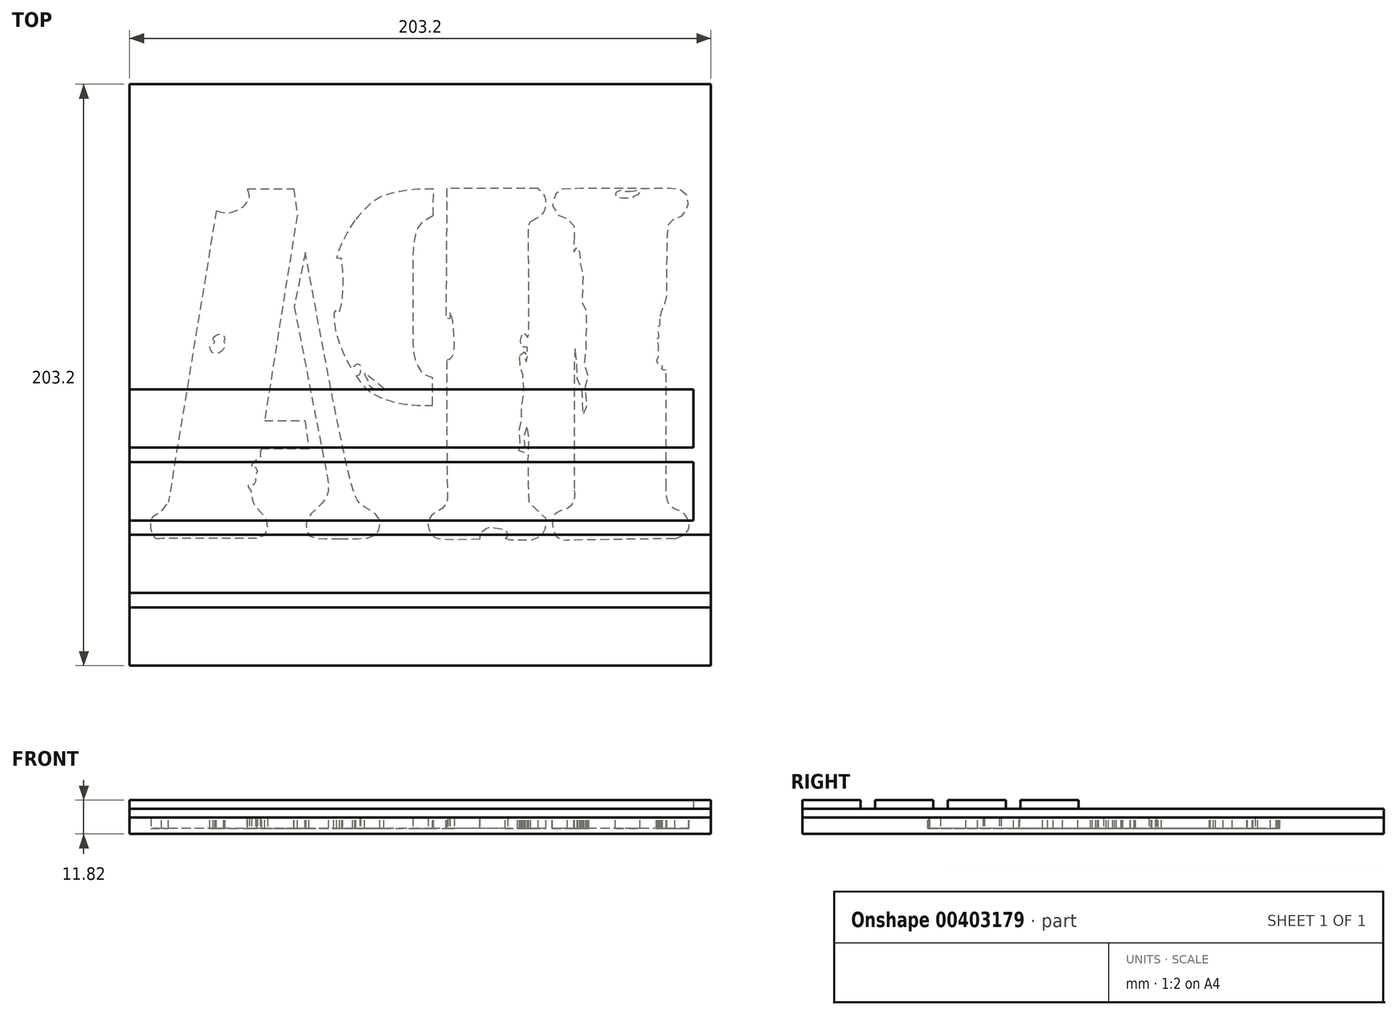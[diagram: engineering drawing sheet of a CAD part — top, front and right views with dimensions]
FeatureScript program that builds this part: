
annotation { "Feature Type Name" : "Feature", "Feature Type Description" : "" }
export const myFeature = defineFeature(function(context is Context, id is Id, definition is map)
    precondition{}
    {
        {
            var Q0;
            Q0=qCreatedBy(makeId("Top.planeOp"),FACE);
            var sketch = newSketch(context, id + "F0", { "sketchPlane" : qUnion([Q0])});
            skFitSpline(sketch, "E0", {"points": [v(8.63, 10.99) * mm, v(3.16, 11.1) * mm, v(2.03, 11.78) * mm, v(1.93, 12.44) * mm, v(2.34, 13.27) * mm, v(3.2, 13.72) * mm, v(3.76, 14.27) * mm, v(3.9, 15.58) * mm], "startDerivative": vector(-23.02, -1.7) * mm, "endDerivative": vector(-0.04, 10.58) * mm});
            skFitSpline(sketch, "E1", {"points": [v(3.9, 15.58) * mm, v(3.9, 25.86) * mm], "startDerivative": vector(0, 10.28) * mm, "endDerivative": vector(0, 10.28) * mm});
            skFitSpline(sketch, "E2", {"points": [v(3.9, 25.86) * mm, v(4.28, 25.86) * mm, v(4.25, 26.1) * mm, v(4.28, 26.25) * mm, v(4.58, 26.3) * mm, v(4.65, 26.5) * mm, v(4.75, 26.69) * mm, v(4.62, 26.85) * mm, v(4.6, 27.18) * mm, v(4.6, 28.18) * mm, v(4.71, 28.29) * mm, v(4.75, 28.5) * mm, v(4.64, 28.62) * mm, v(4.54, 28.64) * mm, v(4.62, 29.55) * mm, v(4.49, 29.68) * mm, v(4.43, 30.53) * mm], "startDerivative": vector(7.22, -1.27) * mm, "endDerivative": vector(-1.81, 11.5) * mm});
            skFitSpline(sketch, "E3", {"points": [v(4.43, 30.53) * mm, v(4.29, 30.67) * mm, v(4.26, 31.3) * mm, v(3.88, 31.92) * mm, v(3.85, 32.16) * mm, v(3.8, 38.07) * mm, v(3.69, 38.6) * mm, v(3.19, 39.04) * mm, v(2.5, 39.32) * mm, v(2.16, 39.77) * mm, v(2.04, 40.1) * mm, v(1.95, 40.63) * mm, v(2.22, 41.22) * mm, v(2.78, 41.61) * mm, v(4.43, 41.68) * mm, v(12.65, 41.66) * mm, v(13.33, 41.46) * mm, v(13.87, 40.49) * mm, v(13.45, 39.44) * mm, v(12.62, 39.1) * mm, v(11.99, 38.46) * mm, v(11.94, 37.56) * mm], "startDerivative": vector(-8.24, 4.86) * mm, "endDerivative": vector(2.02, -20.93) * mm});
            skFitSpline(sketch, "E4", {"points": [v(6.74, 41.43) * mm, v(7.22, 41.4) * mm, v(7.55, 41.4) * mm, v(7.72, 41.44) * mm, v(7.78, 41.5) * mm, v(8.07, 41.45) * mm, v(8.25, 41.38) * mm, v(8.34, 41.07) * mm, v(8.06, 40.91) * mm, v(7.46, 40.87) * mm, v(7.26, 40.88) * mm, v(6.88, 40.91) * mm, v(6.7, 41.04) * mm, v(6.43, 41.13) * mm, v(6.21, 41.4) * mm, v(6.3, 41.54) * mm, v(6.74, 41.43) * mm]});
            skFitSpline(sketch, "E5", {"points": [v(11.94, 37.56) * mm, v(11.94, 36.74) * mm, v(11.94, 35.9) * mm, v(11.69, 36.18) * mm, v(11.67, 36.75) * mm, v(11.47, 36.65) * mm, v(11.48, 35.94) * mm, v(11.38, 35.49) * mm, v(11.4, 35) * mm, v(11.27, 34.69) * mm, v(11.2, 34.18) * mm, v(11.2, 31.64) * mm, v(10.93, 31.4) * mm, v(10.88, 31.03) * mm, v(10.94, 30.22) * mm, v(10.9, 29.85) * mm, v(10.92, 27.74) * mm, v(11.03, 27.64) * mm, v(11.05, 26.28) * mm, v(10.78, 26.1) * mm, v(10.8, 25.13) * mm, v(11.09, 24.86) * mm, v(10.92, 24.19) * mm, v(10.86, 22.69) * mm, v(11.05, 22.44) * mm, v(11.15, 21.9) * mm, v(11.25, 22.13) * mm, v(11.25, 22.95) * mm, v(11.13, 23.3) * mm, v(11.23, 24.02) * mm, v(11.44, 24.54) * mm, v(11.66, 24.84) * mm, v(11.62, 25.64) * mm, v(11.7, 26.18) * mm, v(11.74, 26.82) * mm, v(11.94, 27.99) * mm, v(11.94, 26.88) * mm, v(11.94, 25.42) * mm, v(11.94, 15.3) * mm], "startDerivative": vector(-1.52, -26.45) * mm, "endDerivative": vector(-0.22, -131.99) * mm});
            skFitSpline(sketch, "E6", {"points": [v(11.94, 15.3) * mm, v(11.94, 14.68) * mm, v(12.12, 14.12) * mm, v(12.74, 13.64) * mm, v(13.44, 13.38) * mm, v(13.83, 12.75) * mm, v(13.72, 11.72) * mm, v(13.28, 11.14) * mm, v(12.56, 10.97) * mm], "startDerivative": vector(-0.24, -5.48) * mm, "endDerivative": vector(-6.25, -0.64) * mm});
            skLineSegment(sketch, "E7", {"start": v(3.16, 11.1) * mm, "end": v(12.56, 10.97) * mm});
            skFitSpline(sketch, "E8", {"points": [v(17.99, 11.13) * mm, v(17.76, 11.36) * mm, v(17.85, 11.72) * mm, v(18.56, 11.96) * mm, v(19.35, 12.05) * mm, v(19.85, 11.8) * mm, v(20.16, 11.5) * mm, v(20.2, 11.06) * mm], "startDerivative": vector(-2.5, 1.66) * mm, "endDerivative": vector(-0.24, -3.51) * mm});
            skFitSpline(sketch, "E9", {"points": [v(20.2, 11.06) * mm, v(23.79, 11.06) * mm, v(24.2, 11.28) * mm, v(24.64, 11.93) * mm, v(24.62, 12.74) * mm, v(24.2, 13.36) * mm, v(23.7, 13.6) * mm, v(23.13, 14.1) * mm, v(23, 15.3) * mm, v(23.05, 26.74) * mm], "startDerivative": vector(27, -0.97) * mm, "endDerivative": vector(0, 47.89) * mm});
            skFitSpline(sketch, "E10", {"points": [v(23.05, 26.74) * mm, v(22.7, 26.88) * mm, v(22.45, 27.53) * mm, v(22.44, 28.7) * mm, v(22.51, 29.62) * mm, v(22.69, 30.68) * mm, v(22.81, 30.91) * mm, v(22.83, 30.3) * mm, v(23.16, 30.48) * mm], "startDerivative": vector(-4.05, 0.78) * mm, "endDerivative": vector(5.67, 2.62) * mm});
            skFitSpline(sketch, "E11", {"points": [v(17.99, 11.13) * mm, v(17.99, 11) * mm, v(17.91, 11) * mm, v(15.42, 11) * mm, v(14.79, 11.36) * mm, v(14.5, 11.75) * mm, v(14.45, 12.5) * mm, v(14.5, 13.1) * mm, v(15.69, 13.9) * mm, v(15.91, 14.77) * mm, v(15.96, 18.89) * mm, v(16, 20.94) * mm, v(16.18, 20.94) * mm, v(16.3, 19.13) * mm, v(16.35, 18.42) * mm, v(16.89, 18.99) * mm, v(16.72, 19.3) * mm, v(16.74, 20.57) * mm, v(16.54, 21.5) * mm, v(16.54, 22) * mm, v(16.47, 23.4) * mm, v(16.25, 24.04) * mm, v(16.47, 24.55) * mm, v(16.45, 25.85) * mm, v(16.65, 26.05) * mm, v(16.72, 27.12) * mm], "startDerivative": vector(0.9, -10.65) * mm, "endDerivative": vector(-1.77, 30.67) * mm});
            skFitSpline(sketch, "E12", {"points": [v(16.72, 27.12) * mm, v(16.54, 27.2) * mm, v(16.46, 27.37) * mm, v(16.24, 27.4) * mm, v(16.2, 27.27) * mm, v(16.23, 26.64) * mm, v(16.16, 26.55) * mm, v(16.08, 26.74) * mm, v(16.06, 26.92) * mm, v(16.06, 27.84) * mm, v(16.12, 27.85) * mm, v(16.54, 27.87) * mm, v(16.64, 28.32) * mm, v(16.54, 28.77) * mm, v(16.39, 29.12) * mm, v(16.18, 28.88) * mm, v(16, 28.66) * mm, v(15.9, 29.35) * mm, v(15.95, 38.11) * mm, v(15.75, 38.82) * mm], "startDerivative": vector(-6.43, 1.5) * mm, "endDerivative": vector(-8.8, 2.38) * mm});
            skFitSpline(sketch, "E13", {"points": [v(15.75, 38.82) * mm, v(15.29, 39.07) * mm, v(14.64, 39.58) * mm, v(14.43, 40.24) * mm, v(14.47, 40.93) * mm, v(15.1, 41.7) * mm], "startDerivative": vector(-2.53, 1.33) * mm, "endDerivative": vector(3.33, 3.2) * mm});
            skLineSegment(sketch, "E14", {"start": v(15.1, 41.7) * mm, "end": v(23.08, 41.7) * mm});
            skLineSegment(sketch, "E15", {"start": v(23.08, 41.7) * mm, "end": v(23.16, 30.48) * mm});
            skLineSegment(sketch, "E16", {"start": v(24.26, 39.3) * mm, "end": v(24.24, 41.63) * mm});
            skLineSegment(sketch, "E17", {"start": v(24.32, 22.74) * mm, "end": v(24.32, 25.18) * mm});
            skFitSpline(sketch, "E18", {"points": [v(24.26, 39.3) * mm, v(24.98, 38.89) * mm, v(25.6, 38.28) * mm, v(26, 36.68) * mm, v(26.03, 34.7) * mm, v(26.04, 28.25) * mm, v(25.95, 27.2) * mm, v(25.5, 25.95) * mm, v(24.74, 25.3) * mm, v(24.32, 25.18) * mm], "startDerivative": vector(8.98, -4.32) * mm, "endDerivative": vector(-6.05, -2.55) * mm});
            skFitSpline(sketch, "E19", {"points": [v(24.24, 41.63) * mm, v(25.53, 41.63) * mm, v(27.29, 41.4) * mm, v(29.22, 40.74) * mm, v(31.12, 38.89) * mm], "startDerivative": vector(6.02, 0.18) * mm, "endDerivative": vector(6.03, -7.17) * mm});
            skFitSpline(sketch, "E20", {"points": [v(31.12, 38.89) * mm, v(31.97, 37.5) * mm, v(32.67, 35.56) * mm, v(32.32, 35.64) * mm, v(32.26, 35.27) * mm, v(32.2, 34.51) * mm, v(32.24, 32.03) * mm, v(32.4, 31.15) * mm, v(32.5, 30.86) * mm, v(32.78, 31.08) * mm, v(32.95, 30.3) * mm, v(32.12, 27.3) * mm, v(30.74, 24.94) * mm, v(29.5, 23.75) * mm, v(26.9, 22.87) * mm, v(24.32, 22.74) * mm], "startDerivative": vector(10.41, -15) * mm, "endDerivative": vector(-27.3, 0.19) * mm});
            skFitSpline(sketch, "E21", {"points": [v(32.45, 11.1) * mm, v(29.55, 11.28) * mm, v(28.93, 12.37) * mm, v(29.3, 13.23) * mm, v(30.5, 14) * mm, v(31.25, 15.28) * mm, v(35.44, 36.1) * mm], "startDerivative": vector(-11.08, 1.48) * mm, "endDerivative": vector(10.95, 59.36) * mm});
            skFitSpline(sketch, "E22", {"points": [v(35.44, 36.1) * mm, v(36.41, 31.37) * mm], "startDerivative": vector(0.97, -4.73) * mm, "endDerivative": vector(0.97, -4.73) * mm});
            skFitSpline(sketch, "E23", {"points": [v(36.41, 31.37) * mm, v(33.92, 18.62) * mm, v(33.47, 16.2) * mm, v(33.54, 14.82) * mm, v(34.61, 13.58) * mm, v(35.34, 12.59) * mm, v(35.12, 11.42) * mm, v(32.45, 11.1) * mm], "startDerivative": vector(-10.06, -51.85) * mm, "endDerivative": vector(-34.47, -0.86) * mm});
            skLineSegment(sketch, "E24", {"start": v(40.5, 41.66) * mm, "end": v(36.44, 41.66) * mm});
            skLineSegment(sketch, "E25", {"start": v(36.44, 41.66) * mm, "end": v(36.15, 39.37) * mm});
            skLineSegment(sketch, "E26", {"start": v(36.15, 39.37) * mm, "end": v(39, 21.41) * mm});
            skLineSegment(sketch, "E27", {"start": v(39, 21.41) * mm, "end": v(35.49, 21.41) * mm});
            skLineSegment(sketch, "E28", {"start": v(35.49, 21.41) * mm, "end": v(35.12, 18.92) * mm});
            skLineSegment(sketch, "E29", {"start": v(35.12, 18.92) * mm, "end": v(39.25, 18.92) * mm});
            skLineSegment(sketch, "E30", {"start": v(43.22, 39.76) * mm, "end": v(47.41, 14.28) * mm});
            skFitSpline(sketch, "E31", {"points": [v(39.25, 18.92) * mm, v(39.37, 18.92) * mm, v(39.37, 18.25) * mm, v(39.99, 17.77) * mm, v(40.14, 17.34) * mm, v(39.98, 17.22) * mm, v(39.76, 17.35) * mm, v(39.66, 16.86) * mm, v(39.79, 16.68) * mm, v(39.83, 15.8) * mm, v(40.22, 15.88) * mm, v(40.51, 15.77) * mm, v(40.25, 15.38) * mm, v(40.14, 14.95) * mm, v(40.1, 14.6) * mm, v(39.96, 14.18) * mm, v(39.85, 13.98) * mm, v(39.25, 13.3) * mm, v(38.93, 12.93) * mm, v(38.8, 11.81) * mm, v(39.7, 11.12) * mm], "startDerivative": vector(5.97, 2.03) * mm, "endDerivative": vector(20.28, -1.3) * mm});
            skLineSegment(sketch, "E32", {"start": v(39.7, 11.12) * mm, "end": v(48.01, 11.12) * mm});
            skFitSpline(sketch, "E33", {"points": [v(48.01, 11.12) * mm, v(48.48, 11.12) * mm, v(48.88, 11.78) * mm, v(48.8, 12.95) * mm, v(48.17, 13.4) * mm, v(47.41, 14.28) * mm], "startDerivative": vector(3.3, -0.67) * mm, "endDerivative": vector(-3.06, 4.37) * mm});
            skFitSpline(sketch, "E34", {"points": [v(43.5, 28.54) * mm, v(43.26, 28.84) * mm, v(42.67, 28.93) * mm, v(42.5, 28.48) * mm, v(42.6, 28.32) * mm, v(42.48, 28.17) * mm, v(42.83, 27.4) * mm, v(43.6, 27.39) * mm, v(43.71, 28.04) * mm, v(43.35, 28.25) * mm, v(43.5, 28.54) * mm]});
            skFitSpline(sketch, "E35", {"points": [v(28.57, 24.11) * mm, v(29.8, 25.21) * mm, v(30.26, 25.6) * mm, v(30.2, 25.3) * mm, v(29.97, 24.82) * mm, v(29.93, 24.57) * mm, v(29.48, 24.22) * mm, v(28.99, 24.08) * mm, v(28.57, 24.11) * mm]});
            skFitSpline(sketch, "E36", {"points": [v(31.03, 25.34) * mm, v(30.67, 25.48) * mm, v(30.65, 25.92) * mm, v(30.69, 26.1) * mm, v(30.63, 26.23) * mm, v(31.04, 26.3) * mm, v(31.31, 25.78) * mm], "startDerivative": vector(-2.4, 0.36) * mm, "endDerivative": vector(0.65, -3.12) * mm});
            skFitSpline(sketch, "E37", {"points": [v(43.22, 39.76) * mm, v(42.3, 39.55) * mm, v(41.1, 39.96) * mm, v(40.5, 40.54) * mm, v(40.33, 41) * mm, v(40.5, 41.66) * mm], "startDerivative": vector(-4.01, -1.57) * mm, "endDerivative": vector(1.47, 3.8) * mm});
            skSolve(sketch);
        }
        {
            var Q0;
            Q0=makeQuery(id+"F0.imprint","IMPRINT",FACE,{"disambiguationData":[TD([[makeQuery(id+"F0.imprint","IMPRINT",EDGE,{"derivedFrom":sQuery(id+"F0.wireOp",EDGE,"E0")}),-1.0]])]});
            var Q1;
            Q1=makeQuery(id+"F0.imprint","IMPRINT",FACE,{"disambiguationData":[TD([[makeQuery(id+"F0.imprint","IMPRINT",EDGE,{"derivedFrom":sQuery(id+"F0.wireOp",EDGE,"E8")}),1.0]])]});
            var Q2;
            Q2=makeQuery(id+"F0.imprint","IMPRINT",FACE,{"disambiguationData":[TD([[makeQuery(id+"F0.imprint","IMPRINT",EDGE,{"derivedFrom":sQuery(id+"F0.wireOp",EDGE,"E16")}),-1.0]])]});
            var Q3;
            Q3=makeQuery(id+"F0.imprint","IMPRINT",FACE,{"disambiguationData":[TD([[makeQuery(id+"F0.imprint","IMPRINT",EDGE,{"derivedFrom":sQuery(id+"F0.wireOp",EDGE,"E21")}),-1.0]])]});
            var Q4;
            Q4=makeQuery(id+"F0.imprint","IMPRINT",FACE,{"disambiguationData":[TD([[makeQuery(id+"F0.imprint","IMPRINT",EDGE,{"derivedFrom":sQuery(id+"F0.wireOp",EDGE,"E24")}),1.0]])]});
            extrude(context, id + "F1", {"entities" : qUnion([Q0, Q1, Q2, Q3, Q4]), "depth" : 0.95 * mm});
        }
        {
            var Q0;
            Q0=qCreatedBy(makeId("Top.planeOp"),FACE);
            var sketch = newSketch(context, id + "F2", { "sketchPlane" : qUnion([Q0])});
            skLineSegment(sketch, "E38.bottom", {"start": v(0, 50.8) * mm, "end": v(50.8, 50.8) * mm});
            skLineSegment(sketch, "E38.top", {"start": v(0, 0) * mm, "end": v(50.8, 0) * mm});
            skLineSegment(sketch, "E38.left", {"start": v(0, 50.8) * mm, "end": v(0, 0) * mm});
            skLineSegment(sketch, "E38.right", {"start": v(50.8, 50.8) * mm, "end": v(50.8, 0) * mm});
            skSolve(sketch);
        }
        {
            var Q0;
            Q0 = qSketchRegion(id + "F2", true);
            extrude(context, id + "F3", {"entities" : qUnion([Q0]), "depth" : 1.43 * mm});
        }
        {
            var Q0;
            Q0=makeQuery(id+"F1.opExtrude","SWEPT_BODY",BODY,{"disambiguationData":[OSD([sQuery(id+"F0.wireOp",EDGE,"E0"),sQuery(id+"F0.wireOp",EDGE,"E1"),sQuery(id+"F0.wireOp",EDGE,"E2"),sQuery(id+"F0.wireOp",EDGE,"E3"),sQuery(id+"F0.wireOp",EDGE,"E4"),sQuery(id+"F0.wireOp",EDGE,"E5"),sQuery(id+"F0.wireOp",EDGE,"E6"),sQuery(id+"F0.wireOp",EDGE,"E7")])]});
            var Q1;
            Q1=makeQuery(id+"F1.opExtrude","SWEPT_BODY",BODY,{"disambiguationData":[OSD([sQuery(id+"F0.wireOp",EDGE,"E8"),sQuery(id+"F0.wireOp",EDGE,"E9"),sQuery(id+"F0.wireOp",EDGE,"E10"),sQuery(id+"F0.wireOp",EDGE,"E11"),sQuery(id+"F0.wireOp",EDGE,"E12"),sQuery(id+"F0.wireOp",EDGE,"E13"),sQuery(id+"F0.wireOp",EDGE,"E14"),sQuery(id+"F0.wireOp",EDGE,"E15")])]});
            var Q2;
            Q2=makeQuery(id+"F1.opExtrude","SWEPT_BODY",BODY,{"disambiguationData":[OSD([sQuery(id+"F0.wireOp",EDGE,"E16"),sQuery(id+"F0.wireOp",EDGE,"E17"),sQuery(id+"F0.wireOp",EDGE,"E18"),sQuery(id+"F0.wireOp",EDGE,"E19"),sQuery(id+"F0.wireOp",EDGE,"E20"),sQuery(id+"F0.wireOp",EDGE,"E35"),sQuery(id+"F0.wireOp",EDGE,"E36"),sQuery(id+"F0.wireOp",EDGE,"E20")])]});
            var Q3;
            Q3=makeQuery(id+"F1.opExtrude","SWEPT_BODY",BODY,{"disambiguationData":[OSD([sQuery(id+"F0.wireOp",EDGE,"E21"),sQuery(id+"F0.wireOp",EDGE,"E22"),sQuery(id+"F0.wireOp",EDGE,"E23")])]});
            var Q4;
            Q4=makeQuery(id+"F1.opExtrude","SWEPT_BODY",BODY,{"disambiguationData":[OSD([sQuery(id+"F0.wireOp",EDGE,"E24"),sQuery(id+"F0.wireOp",EDGE,"E25"),sQuery(id+"F0.wireOp",EDGE,"E26"),sQuery(id+"F0.wireOp",EDGE,"E27"),sQuery(id+"F0.wireOp",EDGE,"E28"),sQuery(id+"F0.wireOp",EDGE,"E29"),sQuery(id+"F0.wireOp",EDGE,"E30"),sQuery(id+"F0.wireOp",EDGE,"E31"),sQuery(id+"F0.wireOp",EDGE,"E32"),sQuery(id+"F0.wireOp",EDGE,"E33"),sQuery(id+"F0.wireOp",EDGE,"E34"),sQuery(id+"F0.wireOp",EDGE,"E37")])]});
            var Q5;
            Q5=makeQuery(id+"F3.opExtrude","SWEPT_BODY",BODY,{"disambiguationData":[OSD([sQuery(id+"F2.wireOp",EDGE,"E38.bottom"),sQuery(id+"F2.wireOp",EDGE,"E38.top"),sQuery(id+"F2.wireOp",EDGE,"E38.left"),sQuery(id+"F2.wireOp",EDGE,"E38.right")])]});
            booleanBodies(context, id + "F4", {"operationType" : BooleanOperationType.SUBTRACTION, "tools" : qUnion([Q0, Q1, Q2, Q3, Q4]), "targets" : qUnion([Q5])});
        }
        {
            var Q0;
            Q0=makeQuery(id+"F3.opExtrude","SWEPT_BODY",BODY,{"disambiguationData":[OSD([sQuery(id+"F2.wireOp",EDGE,"E38.bottom"),sQuery(id+"F2.wireOp",EDGE,"E38.top"),sQuery(id+"F2.wireOp",EDGE,"E38.left"),sQuery(id+"F2.wireOp",EDGE,"E38.right")])]});
            var Q1;
            Q1=qCreatedBy(makeId("Origin.pointOp"),VERTEX);
            transform(context, id + "F5", {"entities" : qUnion([Q0]), "transformType" : TransformType.SCALE_UNIFORMLY, "scale" : 4, "scalePoint" : qUnion([Q1]), "makeCopy" : false});
        }
        {
            var Q0;
            Q0=makeQuery(id+"F3.opExtrude","CAP_FACE",FACE,{"disambiguationData":[OSD([sQuery(id+"F2.wireOp",EDGE,"E38.bottom"),sQuery(id+"F2.wireOp",EDGE,"E38.top"),sQuery(id+"F2.wireOp",EDGE,"E38.left"),sQuery(id+"F2.wireOp",EDGE,"E38.right")])],"isStart":false});
            var sketch = newSketch(context, id + "F6", { "sketchPlane" : qUnion([Q0])});
            skLineSegment(sketch, "E39", {"start": v(101.6, 203.2) * mm, "end": v(101.6, 0) * mm, "construction": true});
            skSolve(sketch);
        }
        {
            var Q0;
            Q0=makeQuery(id+"F3.opExtrude","SWEPT_BODY",BODY,{"disambiguationData":[OSD([sQuery(id+"F2.wireOp",EDGE,"E38.bottom"),sQuery(id+"F2.wireOp",EDGE,"E38.top"),sQuery(id+"F2.wireOp",EDGE,"E38.left"),sQuery(id+"F2.wireOp",EDGE,"E38.right")])]});
            var Q1;
            Q1=sQuery(id+"F6.wireOp",EDGE,"E39");
            transform(context, id + "F7", {"entities" : qUnion([Q0]), "transformType" : TransformType.ROTATION, "transformAxis" : qUnion([Q1]), "angle" : 180 * degree, "makeCopy" : false});
        }
        {
            var Q0;
            {var subQ0=sQuery(id+"F2.wireOp",EDGE,"E38.top");var subQ1=sQuery(id+"F2.wireOp",EDGE,"E38.left");var subQ2=sQuery(id+"F2.wireOp",EDGE,"E38.bottom");var subQ3=sQuery(id+"F2.wireOp",EDGE,"E38.right");Q0=makeQuery(id+"F4.opBoolean","SPLIT",FACE,{"disambiguationData":[TD([makeQuery(id+"F1.opExtrude","SWEPT_FACE",FACE,{"disambiguationData":[OSD([sQuery(id+"F0.wireOp",EDGE,"E0")])]})])],"derivedFrom":makeQuery(id+"F3.opExtrude","CAP_FACE",FACE,{"disambiguationData":[OSD([subQ2,subQ0,subQ1,subQ3])],"isStart":true})});}
            var sketch = newSketch(context, id + "F8", { "sketchPlane" : qUnion([Q0])});
            skLineSegment(sketch, "E40.bottom", {"start": v(0, 0) * mm, "end": v(203.2, 0) * mm});
            skLineSegment(sketch, "E40.top", {"start": v(0, 203.2) * mm, "end": v(203.2, 203.2) * mm});
            skLineSegment(sketch, "E40.left", {"start": v(0, 0) * mm, "end": v(0, 203.2) * mm});
            skLineSegment(sketch, "E40.right", {"start": v(203.2, 0) * mm, "end": v(203.2, 203.2) * mm});
            skSolve(sketch);
        }
        {
            var Q0;
            Q0 = qSketchRegion(id + "F8", true);
            extrude(context, id + "F9", {"entities" : qUnion([Q0]), "depth" : 3.05 * mm});
        }
        {
            var Q0;
            Q0=makeQuery(id+"F9.opExtrude","CAP_FACE",FACE,{"disambiguationData":[OSD([sQuery(id+"F8.wireOp",EDGE,"E40.bottom"),sQuery(id+"F8.wireOp",EDGE,"E40.top"),sQuery(id+"F8.wireOp",EDGE,"E40.left"),sQuery(id+"F8.wireOp",EDGE,"E40.right")])],"isStart":false});
            var sketch = newSketch(context, id + "F10", { "sketchPlane" : qUnion([Q0])});
            skLineSegment(sketch, "E41.bottom", {"start": v(0, 0) * mm, "end": v(203.2, 0) * mm});
            skLineSegment(sketch, "E41.top", {"start": v(0, 20.32) * mm, "end": v(203.2, 20.32) * mm});
            skLineSegment(sketch, "E41.left", {"start": v(0, 0) * mm, "end": v(0, 20.32) * mm});
            skLineSegment(sketch, "E41.right", {"start": v(203.2, 0) * mm, "end": v(203.2, 20.32) * mm});
            skLineSegment(sketch, "E42.0.1.0", {"start": v(203.2, 25.4) * mm, "end": v(203.2, 45.72) * mm});
            skLineSegment(sketch, "E42.0.1.1", {"start": v(0, 25.4) * mm, "end": v(0, 45.72) * mm});
            skLineSegment(sketch, "E42.0.1.2", {"start": v(0, 45.72) * mm, "end": v(203.2, 45.72) * mm});
            skLineSegment(sketch, "E42.0.1.3", {"start": v(0, 25.4) * mm, "end": v(203.2, 25.4) * mm});
            skLineSegment(sketch, "E42.0.2.0", {"start": v(197.1, 50.72) * mm, "end": v(197.1, 71.14) * mm});
            skLineSegment(sketch, "E42.0.2.1", {"start": v(0, 50.72) * mm, "end": v(0, 71.14) * mm});
            skLineSegment(sketch, "E42.0.2.2", {"start": v(0, 71.14) * mm, "end": v(197.1, 71.14) * mm});
            skLineSegment(sketch, "E42.0.2.3", {"start": v(0, 50.72) * mm, "end": v(197.1, 50.72) * mm});
            skLineSegment(sketch, "E42.0.3.0", {"start": v(197.1, 76.22) * mm, "end": v(197.1, 96.54) * mm});
            skLineSegment(sketch, "E42.0.3.1", {"start": v(0, 76.22) * mm, "end": v(0, 96.54) * mm});
            skLineSegment(sketch, "E42.0.3.2", {"start": v(0, 96.54) * mm, "end": v(197.1, 96.54) * mm});
            skLineSegment(sketch, "E42.0.3.3", {"start": v(0, 76.22) * mm, "end": v(197.1, 76.22) * mm});
            skLineSegment(sketch, "E42.direction1", {"start": v(0, 0) * mm, "end": v(25.4, 0) * mm, "construction": true});
            skLineSegment(sketch, "E42.direction2", {"start": v(0, 0) * mm, "end": v(0, 25.4) * mm, "construction": true});
            skSolve(sketch);
        }
        {
            var Q0;
            Q0 = qSketchRegion(id + "F10", true);
            extrude(context, id + "F11", {"entities" : qUnion([Q0]), "depth" : 3.05 * mm});
        }
    });
